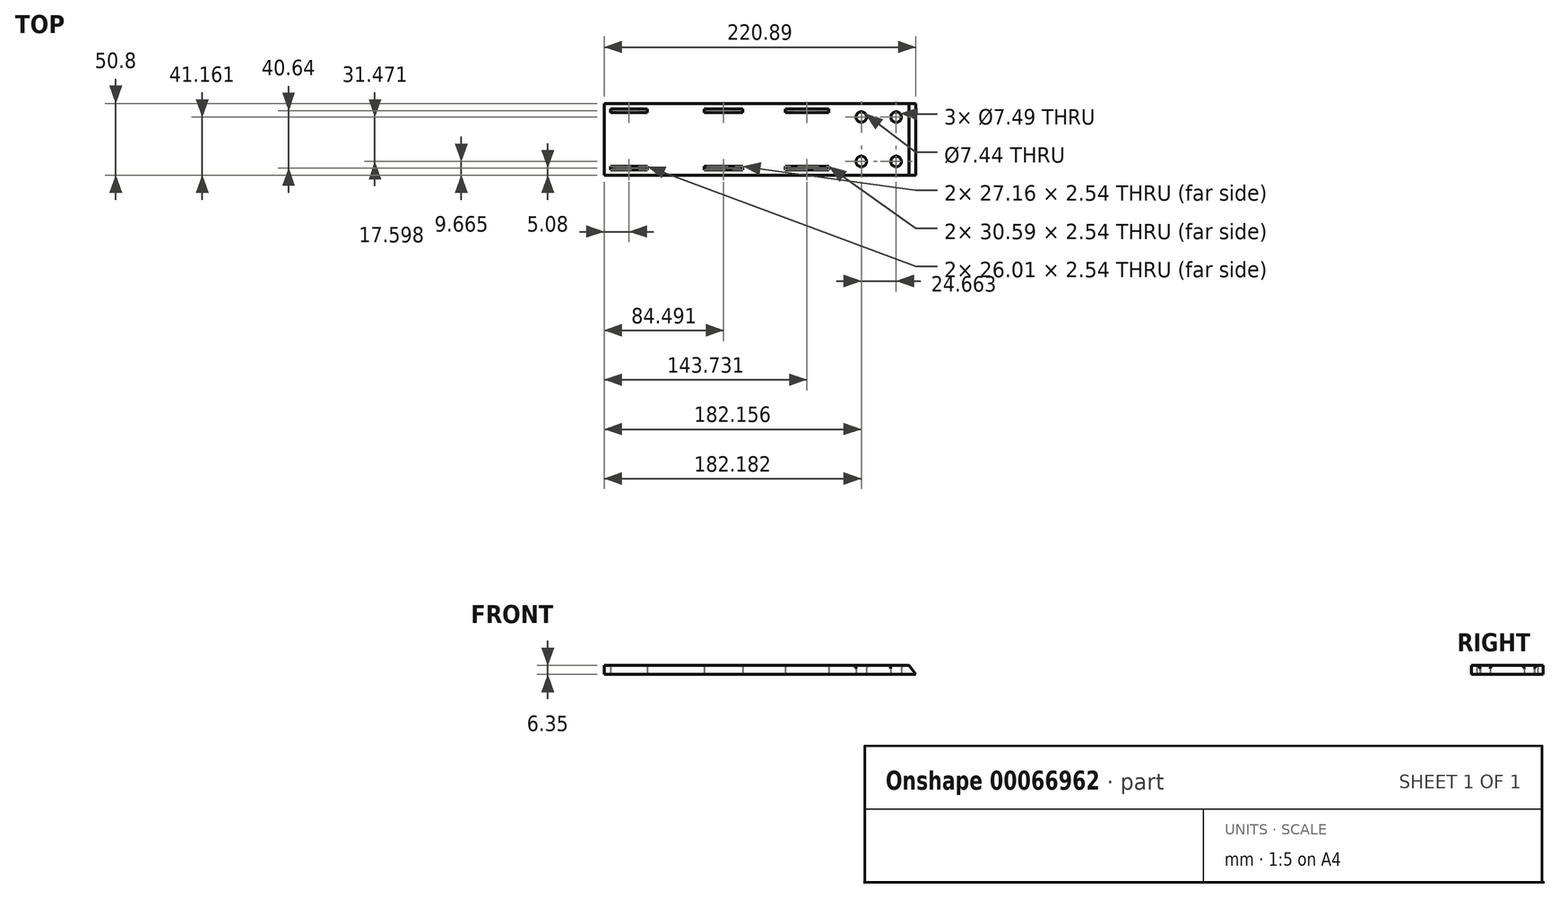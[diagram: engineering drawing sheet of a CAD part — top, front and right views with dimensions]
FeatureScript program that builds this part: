
annotation { "Feature Type Name" : "Feature", "Feature Type Description" : "" }
export const myFeature = defineFeature(function(context is Context, id is Id, definition is map)
    precondition{}
    {
        {
            var Q0;
            Q0=qCreatedBy(makeId("Front.planeOp"),FACE);
            var sketch = newSketch(context, id + "F0", { "sketchPlane" : qUnion([Q0])});
            skLineSegment(sketch, "E0.bottom", {"start": v(-36.4, 99.92) * mm, "end": v(14.4, 99.92) * mm});
            skLineSegment(sketch, "E0.top", {"start": v(-36.4, -115.98) * mm, "end": v(14.4, -115.98) * mm});
            skLineSegment(sketch, "E0.left", {"start": v(-36.4, 99.92) * mm, "end": v(-36.4, -115.98) * mm});
            skLineSegment(sketch, "E0.right", {"start": v(14.4, 99.92) * mm, "end": v(14.4, -115.98) * mm});
            skLineSegment(sketch, "E1.bottom", {"start": v(-32.59, 95.32) * mm, "end": v(-30.05, 95.32) * mm});
            skLineSegment(sketch, "E1.top", {"start": v(-32.59, 69.31) * mm, "end": v(-30.05, 69.31) * mm});
            skLineSegment(sketch, "E1.left", {"start": v(-32.59, 95.32) * mm, "end": v(-32.59, 69.31) * mm});
            skLineSegment(sketch, "E1.right", {"start": v(-30.05, 95.32) * mm, "end": v(-30.05, 69.31) * mm});
            skLineSegment(sketch, "E2.bottom", {"start": v(8.05, 95.32) * mm, "end": v(10.6, 95.32) * mm});
            skLineSegment(sketch, "E2.top", {"start": v(8.05, 69.31) * mm, "end": v(10.6, 69.31) * mm});
            skLineSegment(sketch, "E2.left", {"start": v(8.05, 95.32) * mm, "end": v(8.05, 69.31) * mm});
            skLineSegment(sketch, "E2.right", {"start": v(10.6, 95.32) * mm, "end": v(10.6, 69.31) * mm});
            skLineSegment(sketch, "E3.bottom", {"start": v(-30.05, 29) * mm, "end": v(-32.59, 29) * mm});
            skLineSegment(sketch, "E3.top", {"start": v(-30.05, 1.84) * mm, "end": v(-32.59, 1.84) * mm});
            skLineSegment(sketch, "E3.left", {"start": v(-30.05, 29) * mm, "end": v(-30.05, 1.84) * mm});
            skLineSegment(sketch, "E3.right", {"start": v(-32.59, 29) * mm, "end": v(-32.59, 1.84) * mm});
            skLineSegment(sketch, "E4.bottom", {"start": v(8.05, 29) * mm, "end": v(10.6, 29) * mm});
            skLineSegment(sketch, "E4.top", {"start": v(8.05, 1.84) * mm, "end": v(10.6, 1.84) * mm});
            skLineSegment(sketch, "E4.left", {"start": v(8.05, 29) * mm, "end": v(8.05, 1.84) * mm});
            skLineSegment(sketch, "E4.right", {"start": v(10.6, 29) * mm, "end": v(10.6, 1.84) * mm});
            skLineSegment(sketch, "E5.bottom", {"start": v(-32.59, -28.52) * mm, "end": v(-30.05, -28.52) * mm});
            skLineSegment(sketch, "E5.top", {"start": v(-32.59, -59.1) * mm, "end": v(-30.05, -59.1) * mm});
            skLineSegment(sketch, "E5.left", {"start": v(-32.59, -28.52) * mm, "end": v(-32.59, -59.1) * mm});
            skLineSegment(sketch, "E5.right", {"start": v(-30.05, -28.52) * mm, "end": v(-30.05, -59.1) * mm});
            skLineSegment(sketch, "E6.bottom", {"start": v(8.05, -28.52) * mm, "end": v(10.6, -28.52) * mm});
            skLineSegment(sketch, "E6.top", {"start": v(8.05, -59.1) * mm, "end": v(10.6, -59.1) * mm});
            skLineSegment(sketch, "E6.left", {"start": v(8.05, -28.52) * mm, "end": v(8.05, -59.1) * mm});
            skLineSegment(sketch, "E6.right", {"start": v(10.6, -28.52) * mm, "end": v(10.6, -59.1) * mm});
            skCircle(sketch, "E7", {"center": v(-26.74, -106.9) * mm, "radius": 3.75 * mm});
            skCircle(sketch, "E8", {"center": v(4.74, -106.9) * mm, "radius": 3.75 * mm});
            skCircle(sketch, "E9", {"center": v(-26.74, -82.24) * mm, "radius": 3.75 * mm});
            skCircle(sketch, "E10", {"center": v(4.76, -82.27) * mm, "radius": 3.72 * mm});
            skSolve(sketch);
        }
        {
            var Q0;
            Q0=makeQuery(id+"F0.imprint","IMPRINT",FACE,{"disambiguationData":[TD([[makeQuery(id+"F0.imprint","IMPRINT",EDGE,{"derivedFrom":sQuery(id+"F0.wireOp",EDGE,"E0.bottom")}),-1.0]])]});
            extrude(context, id + "F1", {"entities" : qUnion([Q0]), "depth" : 6.35 * mm});
        }
        {
            var Q0;
            Q0=makeQuery(id+"F1.opExtrude","SWEPT_BODY",BODY,{"disambiguationData":[OSD([sQuery(id+"F0.wireOp",EDGE,"E0.bottom"),sQuery(id+"F0.wireOp",EDGE,"E0.top"),sQuery(id+"F0.wireOp",EDGE,"E0.left"),sQuery(id+"F0.wireOp",EDGE,"E0.right"),sQuery(id+"F0.wireOp",EDGE,"E1.bottom"),sQuery(id+"F0.wireOp",EDGE,"E1.top"),sQuery(id+"F0.wireOp",EDGE,"E1.left"),sQuery(id+"F0.wireOp",EDGE,"E1.right"),sQuery(id+"F0.wireOp",EDGE,"E2.bottom"),sQuery(id+"F0.wireOp",EDGE,"E2.top"),sQuery(id+"F0.wireOp",EDGE,"E2.left"),sQuery(id+"F0.wireOp",EDGE,"E2.right"),sQuery(id+"F0.wireOp",EDGE,"E3.bottom"),sQuery(id+"F0.wireOp",EDGE,"E3.top"),sQuery(id+"F0.wireOp",EDGE,"E3.left"),sQuery(id+"F0.wireOp",EDGE,"E3.right"),sQuery(id+"F0.wireOp",EDGE,"E4.bottom"),sQuery(id+"F0.wireOp",EDGE,"E4.top"),sQuery(id+"F0.wireOp",EDGE,"E4.left"),sQuery(id+"F0.wireOp",EDGE,"E4.right"),sQuery(id+"F0.wireOp",EDGE,"E5.bottom"),sQuery(id+"F0.wireOp",EDGE,"E5.top"),sQuery(id+"F0.wireOp",EDGE,"E5.left"),sQuery(id+"F0.wireOp",EDGE,"E5.right"),sQuery(id+"F0.wireOp",EDGE,"E6.bottom"),sQuery(id+"F0.wireOp",EDGE,"E6.top"),sQuery(id+"F0.wireOp",EDGE,"E6.left"),sQuery(id+"F0.wireOp",EDGE,"E6.right")])]});
            var Q1;
            Q1=makeQuery(id+"F1.opExtrude","CAP_EDGE",EDGE,{"disambiguationData":[OSD([sQuery(id+"F0.wireOp",EDGE,"E0.bottom")])],"isStart":true});
            transform(context, id + "F2", {"entities" : qUnion([Q0]), "transformType" : TransformType.ROTATION, "transformAxis" : qUnion([Q1]), "angle" : 180 * degree, "makeCopy" : false});
        }
        {
            var Q0;
            Q0=makeQuery(id+"F1.opExtrude","SWEPT_FACE",FACE,{"disambiguationData":[OSD([sQuery(id+"F0.wireOp",EDGE,"E0.right")])]});
            var sketch = newSketch(context, id + "F3", { "sketchPlane" : qUnion([Q0])});
            skLineSegment(sketch, "E11", {"start": v(0, 315.82) * mm, "end": v(0, 320.8) * mm});
            skLineSegment(sketch, "E12", {"start": v(0, 320.8) * mm, "end": v(6.35, 315.82) * mm});
            skSolve(sketch);
        }
        {
            var Q0;
            Q0=makeQuery(id+"F3.imprint","IMPRINT",FACE,{"disambiguationData":[TD([[makeQuery(id+"F3.imprint","IMPRINT",EDGE,{"derivedFrom":sQuery(id+"F3.wireOp",EDGE,"E11")}),-1.0]])]});
            extrude(context, id + "F4", {"entities" : qUnion([Q0]), "operationType" : NewBodyOperationType.ADD, "oppositeDirection" : true, "depth" : 50.8 * mm});
        }
        {
            var Q0;
            Q0=makeQuery(id+"F1.opExtrude","SWEPT_BODY",BODY,{"disambiguationData":[OSD([sQuery(id+"F0.wireOp",EDGE,"E0.bottom"),sQuery(id+"F0.wireOp",EDGE,"E0.top"),sQuery(id+"F0.wireOp",EDGE,"E0.left"),sQuery(id+"F0.wireOp",EDGE,"E0.right"),sQuery(id+"F0.wireOp",EDGE,"E1.bottom"),sQuery(id+"F0.wireOp",EDGE,"E1.top"),sQuery(id+"F0.wireOp",EDGE,"E1.left"),sQuery(id+"F0.wireOp",EDGE,"E1.right"),sQuery(id+"F0.wireOp",EDGE,"E2.bottom"),sQuery(id+"F0.wireOp",EDGE,"E2.top"),sQuery(id+"F0.wireOp",EDGE,"E2.left"),sQuery(id+"F0.wireOp",EDGE,"E2.right"),sQuery(id+"F0.wireOp",EDGE,"E3.bottom"),sQuery(id+"F0.wireOp",EDGE,"E3.top"),sQuery(id+"F0.wireOp",EDGE,"E3.left"),sQuery(id+"F0.wireOp",EDGE,"E3.right"),sQuery(id+"F0.wireOp",EDGE,"E4.bottom"),sQuery(id+"F0.wireOp",EDGE,"E4.top"),sQuery(id+"F0.wireOp",EDGE,"E4.left"),sQuery(id+"F0.wireOp",EDGE,"E4.right"),sQuery(id+"F0.wireOp",EDGE,"E5.bottom"),sQuery(id+"F0.wireOp",EDGE,"E5.top"),sQuery(id+"F0.wireOp",EDGE,"E5.left"),sQuery(id+"F0.wireOp",EDGE,"E5.right"),sQuery(id+"F0.wireOp",EDGE,"E6.bottom"),sQuery(id+"F0.wireOp",EDGE,"E6.top"),sQuery(id+"F0.wireOp",EDGE,"E6.left"),sQuery(id+"F0.wireOp",EDGE,"E6.right"),sQuery(id+"F0.wireOp",EDGE,"E7"),sQuery(id+"F0.wireOp",EDGE,"E8"),sQuery(id+"F0.wireOp",EDGE,"E9"),sQuery(id+"F0.wireOp",EDGE,"E10")])]});
            var Q1;
            Q1=makeQuery(id+"F1.opExtrude","CAP_EDGE",EDGE,{"disambiguationData":[OSD([sQuery(id+"F0.wireOp",EDGE,"E0.bottom")])],"isStart":true});
            transform(context, id + "F5", {"entities" : qUnion([Q0]), "transformType" : TransformType.ROTATION, "transformAxis" : qUnion([Q1]), "angle" : 90 * degree, "makeCopy" : false});
        }
        {
            var Q0;
            Q0=makeQuery(id+"F1.opExtrude","SWEPT_BODY",BODY,{"disambiguationData":[OSD([sQuery(id+"F0.wireOp",EDGE,"E0.bottom"),sQuery(id+"F0.wireOp",EDGE,"E0.top"),sQuery(id+"F0.wireOp",EDGE,"E0.left"),sQuery(id+"F0.wireOp",EDGE,"E0.right"),sQuery(id+"F0.wireOp",EDGE,"E1.bottom"),sQuery(id+"F0.wireOp",EDGE,"E1.top"),sQuery(id+"F0.wireOp",EDGE,"E1.left"),sQuery(id+"F0.wireOp",EDGE,"E1.right"),sQuery(id+"F0.wireOp",EDGE,"E2.bottom"),sQuery(id+"F0.wireOp",EDGE,"E2.top"),sQuery(id+"F0.wireOp",EDGE,"E2.left"),sQuery(id+"F0.wireOp",EDGE,"E2.right"),sQuery(id+"F0.wireOp",EDGE,"E3.bottom"),sQuery(id+"F0.wireOp",EDGE,"E3.top"),sQuery(id+"F0.wireOp",EDGE,"E3.left"),sQuery(id+"F0.wireOp",EDGE,"E3.right"),sQuery(id+"F0.wireOp",EDGE,"E4.bottom"),sQuery(id+"F0.wireOp",EDGE,"E4.top"),sQuery(id+"F0.wireOp",EDGE,"E4.left"),sQuery(id+"F0.wireOp",EDGE,"E4.right"),sQuery(id+"F0.wireOp",EDGE,"E5.bottom"),sQuery(id+"F0.wireOp",EDGE,"E5.top"),sQuery(id+"F0.wireOp",EDGE,"E5.left"),sQuery(id+"F0.wireOp",EDGE,"E5.right"),sQuery(id+"F0.wireOp",EDGE,"E6.bottom"),sQuery(id+"F0.wireOp",EDGE,"E6.top"),sQuery(id+"F0.wireOp",EDGE,"E6.left"),sQuery(id+"F0.wireOp",EDGE,"E6.right"),sQuery(id+"F0.wireOp",EDGE,"E7"),sQuery(id+"F0.wireOp",EDGE,"E8"),sQuery(id+"F0.wireOp",EDGE,"E9"),sQuery(id+"F0.wireOp",EDGE,"E10")])]});
            var Q1;
            Q1=makeQuery(id+"F1.opExtrude","SWEPT_EDGE",EDGE,{"disambiguationData":[OSD([sQuery(id+"F0.wireOp",EDGE,"E0.bottom"),sQuery(id+"F0.wireOp",EDGE,"E0.right")])]});
            transform(context, id + "F6", {"entities" : qUnion([Q0]), "transformType" : TransformType.ROTATION, "transformAxis" : qUnion([Q1]), "angle" : 90 * degree, "oppositeDirection" : true, "makeCopy" : false});
        }
        {
            var Q0;
            Q0=makeQuery(id+"F1.opExtrude","CAP_EDGE",EDGE,{"disambiguationData":[OSD([sQuery(id+"F0.wireOp",EDGE,"E10")])],"isStart":false});
            var Q1;
            Q1=makeQuery(id+"F1.opExtrude","CAP_EDGE",EDGE,{"disambiguationData":[OSD([sQuery(id+"F0.wireOp",EDGE,"E8")])],"isStart":false});
            var Q2;
            Q2=makeQuery(id+"F1.opExtrude","CAP_EDGE",EDGE,{"disambiguationData":[OSD([sQuery(id+"F0.wireOp",EDGE,"E9")])],"isStart":false});
            var Q3;
            Q3=makeQuery(id+"F1.opExtrude","CAP_EDGE",EDGE,{"disambiguationData":[OSD([sQuery(id+"F0.wireOp",EDGE,"E7")])],"isStart":false});
            fillet(context, id + "F7", {"entities" : qUnion([Q0, Q1, Q2, Q3]), "radius" : 2.3 * mm, "tangentPropagation" : true, "allowEdgeOverflow" : false});
        }
    });
